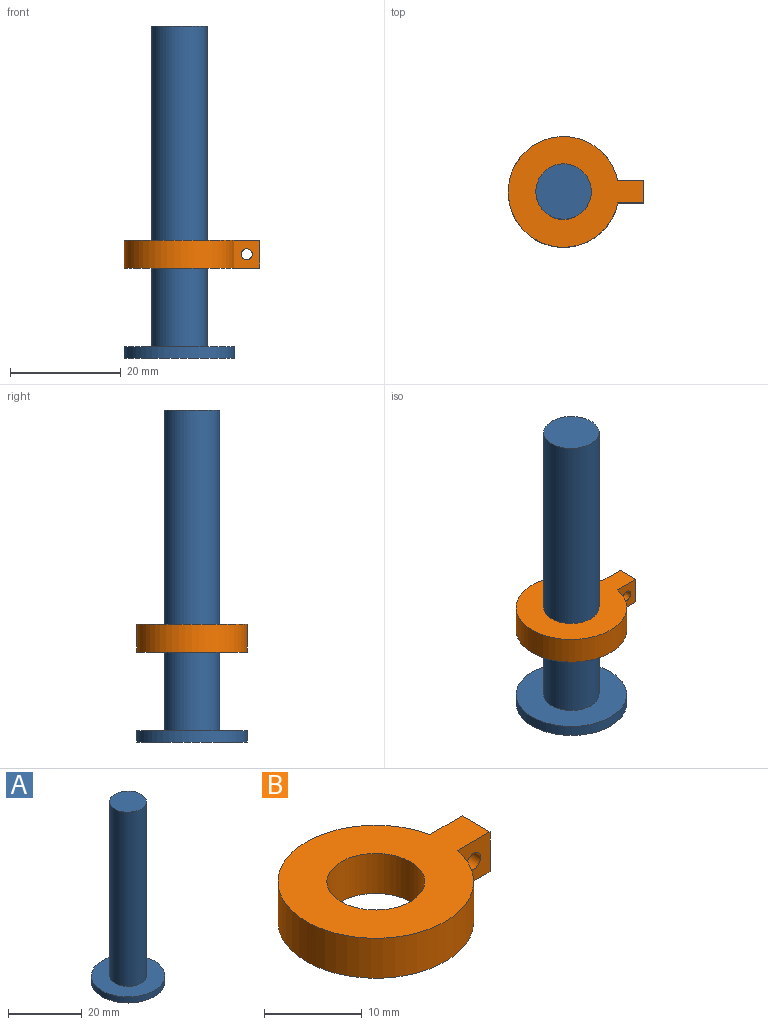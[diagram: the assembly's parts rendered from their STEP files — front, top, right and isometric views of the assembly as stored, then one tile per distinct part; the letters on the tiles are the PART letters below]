
ASSEMBLY  parts=2 mates=1
PART A: 5 faces, bbox 20x20x60 mm
  f0: plane 10x10mm, normal (0,0,1), area 78.5mm2, adj f1
  f1: cylinder r=5mm len=58mm, axis (0,0,1), area 1822.1mm2, adj f0,f3
  f2: cylinder r=10mm len=20mm, axis (0,0,-1), area 125.7mm2, adj f3,f4
  f3: plane 20x20mm, normal (0,0,1), area 235.6mm2, adj f1,f2
  f4: plane 20x20mm, normal (0,0,-1), area 314.2mm2, adj f2
PART B: 8 faces, bbox 24.5x20x5 mm
  f0: cylinder r=10mm len=20mm, axis (0,0,-1), area 294mm2, adj f2,f3,f4,f5
  f1: cylinder r=5mm len=10mm, axis (0,0,-1), area 157.1mm2, adj f2,f3
  f2: plane 24.5x20mm, normal (0,0,1), area 253.9mm2, adj f0,f1,f4,f5,f6
  f3: plane 24.5x20mm, normal (0,0,-1), area 253.9mm2, adj f0,f1,f4,f5,f6
  f4: plane 5x4.7mm, normal (0,-1,0), area 20.4mm2, adj f0,f2,f3,f6,f7
  f5: plane 5x4.7mm, normal (0,1,0), area 20.4mm2, adj f0,f2,f3,f6,f7
  f6: plane 5x4mm, normal (1,0,0), area 20mm2, adj f2,f3,f4,f5
  f7: cylinder r=1mm len=4mm, axis (0,-1,0), area 25.1mm2, adj f4,f5
PLACE A at identity fixed
PLACE B t=(0,0,14.25)mm
MATE slider B.f1 <-> A.f1  axis (0,0,1) through (0,0,21.25)mm
